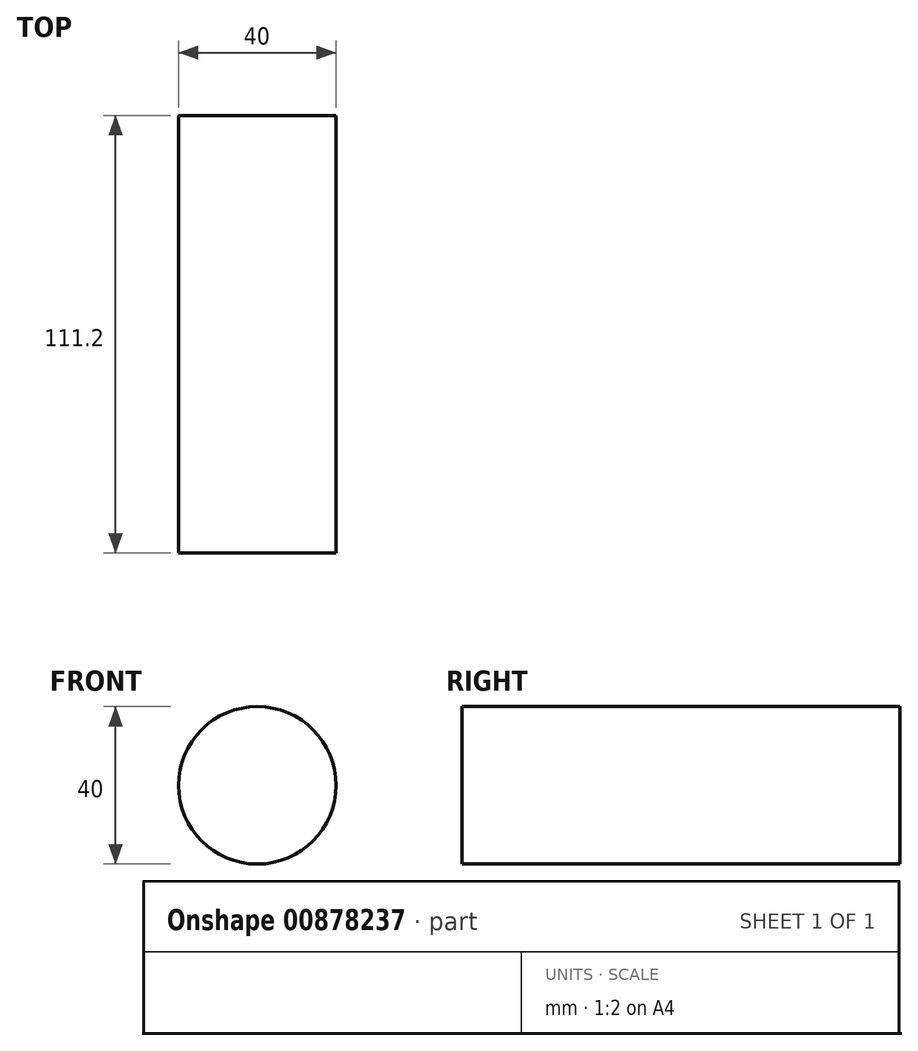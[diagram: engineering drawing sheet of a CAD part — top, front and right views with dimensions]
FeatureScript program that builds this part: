
annotation { "Feature Type Name" : "Feature", "Feature Type Description" : "" }
export const myFeature = defineFeature(function(context is Context, id is Id, definition is map)
    precondition{}
    {
        {
            var Q0;
            Q0=qCreatedBy(makeId("Front.planeOp"),FACE);
            var sketch = newSketch(context, id + "F0", { "sketchPlane" : qUnion([Q0])});
            skCircle(sketch, "E0", {"center": v(0, 0) * mm, "radius": 20 * mm});
            skSolve(sketch);
        }
        {
            var Q0;
            Q0 = qSketchRegion(id + "F0", true);
            extrude(context, id + "F1", {"entities" : qUnion([Q0]), "depth" : 111.2 * mm, "offsetDistance" : 25 * mm});
        }
    });
